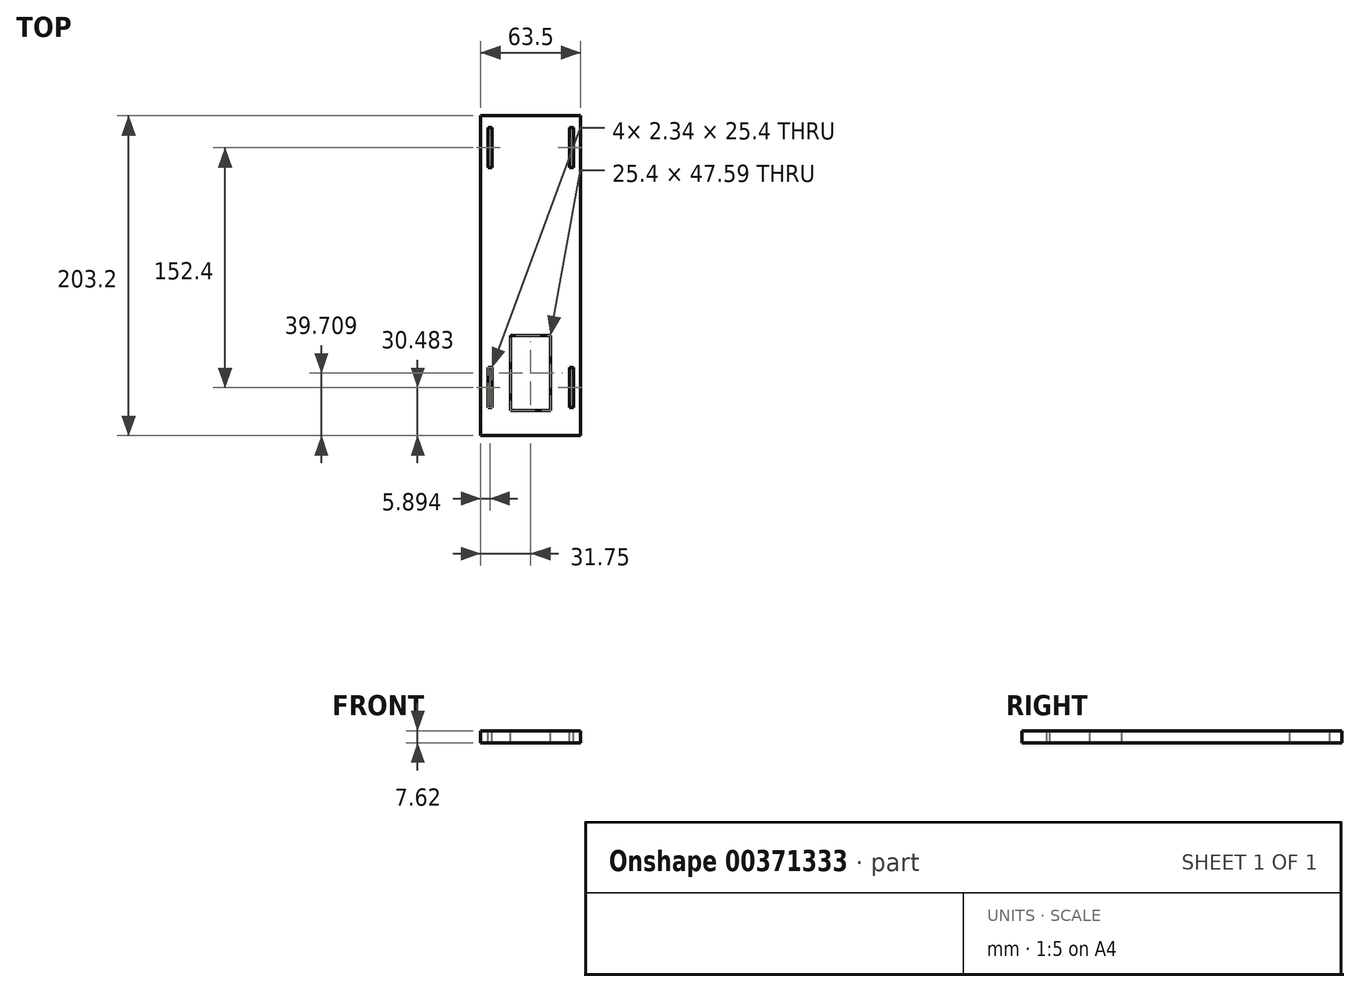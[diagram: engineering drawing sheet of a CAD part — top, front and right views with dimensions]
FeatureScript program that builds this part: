
annotation { "Feature Type Name" : "Feature", "Feature Type Description" : "" }
export const myFeature = defineFeature(function(context is Context, id is Id, definition is map)
    precondition{}
    {
        {
            var Q0;
            Q0=qCreatedBy(makeId("Top.planeOp"),FACE);
            var sketch = newSketch(context, id + "F0", { "sketchPlane" : qUnion([Q0])});
            skLineSegment(sketch, "E0", {"start": v(-63.5, -75.58) * mm, "end": v(-63.5, 127.62) * mm});
            skLineSegment(sketch, "E1", {"start": v(-63.5, 127.62) * mm, "end": v(0, 127.62) * mm});
            skLineSegment(sketch, "E2", {"start": v(0, 127.62) * mm, "end": v(0, -75.58) * mm});
            skLineSegment(sketch, "E3", {"start": v(0, -75.58) * mm, "end": v(-63.5, -75.58) * mm});
            skSolve(sketch);
        }
        {
            var Q0;
            Q0 = qSketchRegion(id + "F0", true);
            extrude(context, id + "F1", {"entities" : qUnion([Q0]), "depth" : 7.62 * mm});
        }
        {
            var Q0;
            Q0=makeQuery(id+"F1.opExtrude","CAP_FACE",FACE,{"disambiguationData":[OSD([sQuery(id+"F0.wireOp",EDGE,"E0"),sQuery(id+"F0.wireOp",EDGE,"E1"),sQuery(id+"F0.wireOp",EDGE,"E2"),sQuery(id+"F0.wireOp",EDGE,"E3")])],"isStart":false});
            var sketch = newSketch(context, id + "F2", { "sketchPlane" : qUnion([Q0])});
            skLineSegment(sketch, "E4", {"start": v(-19.05, -12.08) * mm, "end": v(-44.45, -12.08) * mm});
            skLineSegment(sketch, "E5", {"start": v(-31.75, -12.08) * mm, "end": v(-44.45, -12.08) * mm});
            skLineSegment(sketch, "E6", {"start": v(-44.45, -12.08) * mm, "end": v(-44.45, -59.67) * mm});
            skLineSegment(sketch, "E7", {"start": v(-44.45, -59.67) * mm, "end": v(-44.45, -12.08) * mm});
            skLineSegment(sketch, "E8", {"start": v(-19.05, -12.08) * mm, "end": v(-19.05, -59.67) * mm});
            skLineSegment(sketch, "E9", {"start": v(-19.05, -59.67) * mm, "end": v(-44.45, -59.67) * mm});
            skPoint(sketch, "E10.end.orphan", {"position": v(-31.75, -43.83) * mm});
            skPoint(sketch, "E11.start.orphan", {"position": v(-31.75, -75.58) * mm});
            skPoint(sketch, "E12.orphan", {"position": v(0, -12.08) * mm});
            skPoint(sketch, "E13.start.orphan", {"position": v(-63.5, -12.08) * mm});
            skPoint(sketch, "E14.orphan", {"position": v(-63.5, -75.58) * mm});
            skPoint(sketch, "E15.end.orphan", {"position": v(0, -75.58) * mm});
            skSolve(sketch);
        }
        {
            var Q0;
            Q0 = qSketchRegion(id + "F2", true);
            extrude(context, id + "F3", {"entities" : qUnion([Q0]), "operationType" : NewBodyOperationType.REMOVE, "oppositeDirection" : true, "depth" : 12.7 * mm});
        }
        {
            var Q0;
            Q0=makeQuery(id+"F1.opExtrude","CAP_FACE",FACE,{"disambiguationData":[OSD([sQuery(id+"F0.wireOp",EDGE,"E0"),sQuery(id+"F0.wireOp",EDGE,"E1"),sQuery(id+"F0.wireOp",EDGE,"E2"),sQuery(id+"F0.wireOp",EDGE,"E3")])],"isStart":false});
            var sketch = newSketch(context, id + "F4", { "sketchPlane" : qUnion([Q0])});
            skLineSegment(sketch, "E16.bottom", {"start": v(-58.77, 120) * mm, "end": v(-56.44, 120) * mm});
            skLineSegment(sketch, "E16.top", {"start": v(-58.77, 94.6) * mm, "end": v(-56.44, 94.6) * mm});
            skLineSegment(sketch, "E16.left", {"start": v(-58.77, 120) * mm, "end": v(-58.77, 94.6) * mm});
            skLineSegment(sketch, "E16.right", {"start": v(-56.44, 120) * mm, "end": v(-56.44, 94.6) * mm});
            skLineSegment(sketch, "E17.bottom", {"start": v(-58.78, -57.8) * mm, "end": v(-56.44, -57.8) * mm});
            skLineSegment(sketch, "E17.top", {"start": v(-58.78, -32.4) * mm, "end": v(-56.44, -32.4) * mm});
            skLineSegment(sketch, "E17.left", {"start": v(-58.78, -57.8) * mm, "end": v(-58.78, -32.4) * mm});
            skLineSegment(sketch, "E17.right", {"start": v(-56.44, -57.8) * mm, "end": v(-56.44, -32.4) * mm});
            skLineSegment(sketch, "E18", {"start": v(-31.75, 127.62) * mm, "end": v(-31.75, 42) * mm, "construction": true});
            skLineSegment(sketch, "E19.MirrorCS", {"start": v(-7.06, 120) * mm, "end": v(-7.06, 94.6) * mm});
            skLineSegment(sketch, "E20.MirrorCS", {"start": v(-4.73, 94.6) * mm, "end": v(-7.06, 94.6) * mm});
            skLineSegment(sketch, "E21.MirrorCS", {"start": v(-4.73, 120) * mm, "end": v(-4.73, 94.6) * mm});
            skLineSegment(sketch, "E22.MirrorCS", {"start": v(-4.73, 120) * mm, "end": v(-7.06, 120) * mm});
            skLineSegment(sketch, "E23.MirrorCS", {"start": v(-4.72, -57.8) * mm, "end": v(-7.06, -57.8) * mm});
            skLineSegment(sketch, "E24.MirrorCS", {"start": v(-7.06, -57.8) * mm, "end": v(-7.06, -32.4) * mm});
            skLineSegment(sketch, "E25.MirrorCS", {"start": v(-4.72, -32.4) * mm, "end": v(-7.06, -32.4) * mm});
            skLineSegment(sketch, "E26.MirrorCS", {"start": v(-4.72, -57.8) * mm, "end": v(-4.72, -32.4) * mm});
            skSolve(sketch);
        }
        {
            var Q0;
            Q0 = qSketchRegion(id + "F4", true);
            extrude(context, id + "F5", {"entities" : qUnion([Q0]), "operationType" : NewBodyOperationType.REMOVE, "oppositeDirection" : true, "depth" : 25.4 * mm});
        }
    });
